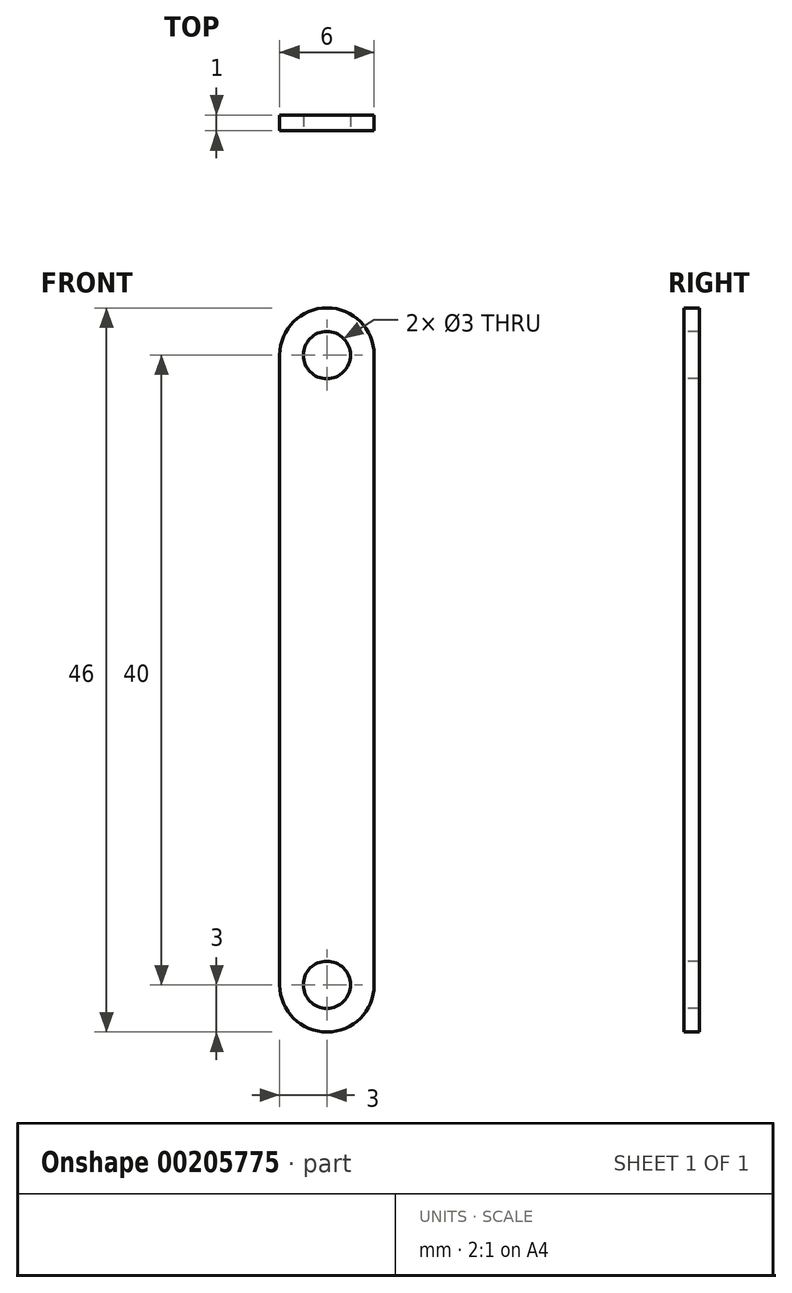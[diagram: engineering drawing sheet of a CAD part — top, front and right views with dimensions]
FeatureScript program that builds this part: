
annotation { "Feature Type Name" : "Feature", "Feature Type Description" : "" }
export const myFeature = defineFeature(function(context is Context, id is Id, definition is map)
    precondition{}
    {
        {
            var Q0;
            Q0=qCreatedBy(makeId("Front.planeOp"),FACE);
            var sketch = newSketch(context, id + "F0", { "sketchPlane" : qUnion([Q0])});
            skLineSegment(sketch, "E0", {"start": v(0, 0) * mm, "end": v(0, -40) * mm, "construction": true});
            skCircle(sketch, "E1", {"center": v(0, 0) * mm, "radius": 1.5 * mm});
            skCircle(sketch, "E2", {"center": v(0, -40) * mm, "radius": 1.5 * mm});
            skArc(sketch, "E3.0.startCap", {"start": v(-3, 0) * mm, "mid": v(0, 3) * mm, "end": v(3, 0) * mm});
            skArc(sketch, "E3.0.endCap", {"start": v(3, -40) * mm, "mid": v(0, -43) * mm, "end": v(-3, -40) * mm});
            skLineSegment(sketch, "E3.0.left", {"start": v(3, 0) * mm, "end": v(3, -40) * mm});
            skLineSegment(sketch, "E3.0.right", {"start": v(-3, 0) * mm, "end": v(-3, -40) * mm});
            skSolve(sketch);
        }
        {
            var Q0;
            Q0 = qSketchRegion(id + "F0", true);
            extrude(context, id + "F1", {"entities" : qUnion([Q0]), "oppositeDirection" : true, "depth" : 1 * mm});
        }
    });
